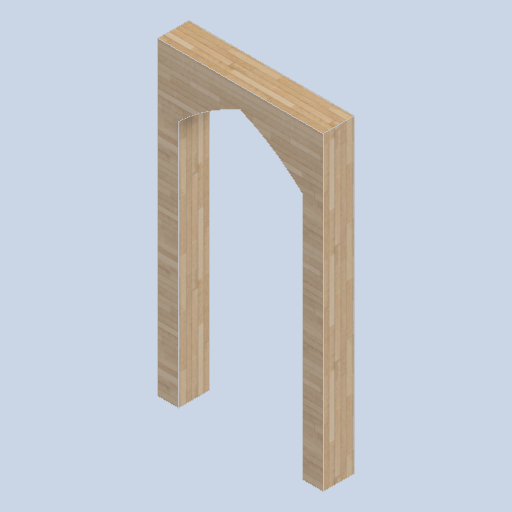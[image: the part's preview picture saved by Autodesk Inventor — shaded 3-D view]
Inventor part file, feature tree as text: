
AUTODESK INVENTOR PART (.ipt)
format: ipt  version: 2024.2 (Build 282272000, 272)  size: 187,392 bytes
history: native  units: in
note: dims shown in document units (in); Inventor stores cm internally (conversion verified against a paired STEP export)
features: other x3, sketch x2
ambient origin geometry x8: Origin, YZ Plane, XZ Plane, XY Plane, X Axis, Y Axis, Z Axis, Center Point
bodies: Solid1 (feature_tree)
feature tree (5):
  other  "front_wall_block06.ipt"
  other  "Solid1::front_wall_block06.ipt"
  other  "TaggingFeature1"
  sketch  "Sketch1"  dims[d0=0.3937in]
  sketch  "Sketch2"
